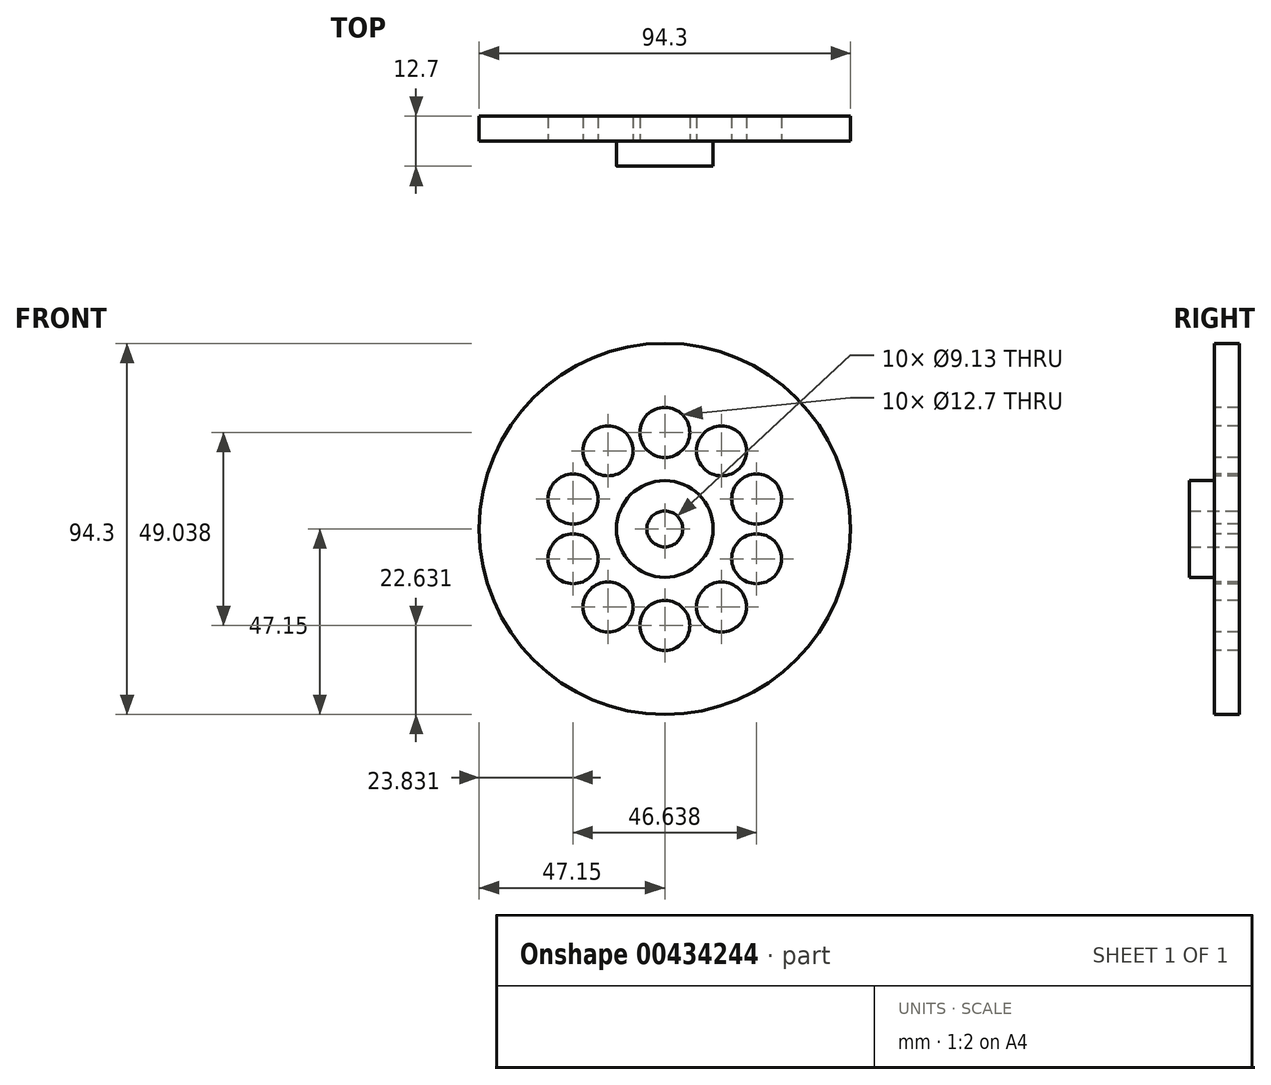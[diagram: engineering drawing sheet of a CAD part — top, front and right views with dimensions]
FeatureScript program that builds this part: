
annotation { "Feature Type Name" : "Feature", "Feature Type Description" : "" }
export const myFeature = defineFeature(function(context is Context, id is Id, definition is map)
    precondition{}
    {
        {
            var Q0;
            Q0=qCreatedBy(makeId("Front.planeOp"),FACE);
            var sketch = newSketch(context, id + "F0", { "sketchPlane" : qUnion([Q0])});
            skCircle(sketch, "E0", {"center": v(0, 0) * mm, "radius": 47.15 * mm});
            skCircle(sketch, "E1", {"center": v(0, 0) * mm, "radius": 12.28 * mm});
            skCircle(sketch, "E2", {"center": v(0, 0) * mm, "radius": 4.56 * mm});
            skSolve(sketch);
        }
        {
            var Q0;
            Q0=makeQuery(id+"F0.imprint","IMPRINT",FACE,{"disambiguationData":[TD([[makeQuery(id+"F0.imprint","IMPRINT",EDGE,{"derivedFrom":sQuery(id+"F0.wireOp",EDGE,"E0")}),1.0]])]});
            extrude(context, id + "F1", {"entities" : qUnion([Q0]), "depth" : 6.35 * mm});
        }
        {
            var Q0;
            Q0=makeQuery(id+"F0.imprint","IMPRINT",FACE,{"disambiguationData":[TD([[makeQuery(id+"F0.imprint","IMPRINT",EDGE,{"derivedFrom":sQuery(id+"F0.wireOp",EDGE,"E1")}),1.0]])]});
            extrude(context, id + "F2", {"entities" : qUnion([Q0]), "operationType" : NewBodyOperationType.ADD, "depth" : 12.7 * mm});
        }
        {
            var Q0;
            Q0=makeQuery(id+"F1.opExtrude","CAP_FACE",FACE,{"disambiguationData":[OSD([sQuery(id+"F0.wireOp",EDGE,"E0"),sQuery(id+"F0.wireOp",EDGE,"E1")])],"isStart":false});
            var sketch = newSketch(context, id + "F3", { "sketchPlane" : qUnion([Q0])});
            skLineSegment(sketch, "E3", {"start": v(0, 0) * mm, "end": v(0, 24.52) * mm});
            skSolve(sketch);
        }
        {
            var Q0;
            Q0=sQuery(id+"F3.wireOp",VERTEX,"E3.end");
            var Q1;
            Q1=makeQuery(id+"F1.opExtrude","SWEPT_BODY",BODY,{"disambiguationData":[OSD([sQuery(id+"F0.wireOp",EDGE,"E0"),sQuery(id+"F0.wireOp",EDGE,"E1")])]});
            hole(context, id + "F4", {"style" : HoleStyle.SIMPLE, "endStyle" : HoleEndStyle.THROUGH, "holeDiameter" : 12.7 * mm, "isTappedThrough" : true, "tappedDepth" : 12.7 * mm, "tapClearance" : 3, "locations" : qUnion([Q0]), "scope" : qUnion([Q1])});
        }
        {
            var Q0;
            Q0=makeQuery(id+"F1.opExtrude","SWEPT_BODY",BODY,{"disambiguationData":[OSD([sQuery(id+"F0.wireOp",EDGE,"E0"),sQuery(id+"F0.wireOp",EDGE,"E1")])]});
            var Q1;
            Q1=makeQuery(id+"F2.opExtrude","SWEPT_FACE",FACE,{"disambiguationData":[OSD([sQuery(id+"F0.wireOp",EDGE,"E2")])]});
            circularPattern(context, id + "F5", {"entities" : qUnion([Q0]), "axis" : qUnion([Q1]), "angle" : 360 * degree, "instanceCount" : 10, "equalSpace" : true});
        }
    });
